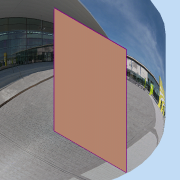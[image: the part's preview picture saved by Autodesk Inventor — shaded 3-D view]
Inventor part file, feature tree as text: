
AUTODESK INVENTOR PART (.ipt)
format: ipt  version: 2019 (Build 230136000, 136)  size: 125,440 bytes
history: native  units: mm
features: other x1, extrude x1, sketch x1
ambient origin geometry x8: Origin, YZ Plane, XZ Plane, XY Plane, X Axis, Y Axis, Z Axis, Center Point
bodies: Body1 (feature_tree)
feature tree (3):
  other  "Твердое тело1"
  extrude  "Выдавливание1"  Depth=29311.5mm TaperAngle=0.0deg
  sketch  "Эскиз1"
